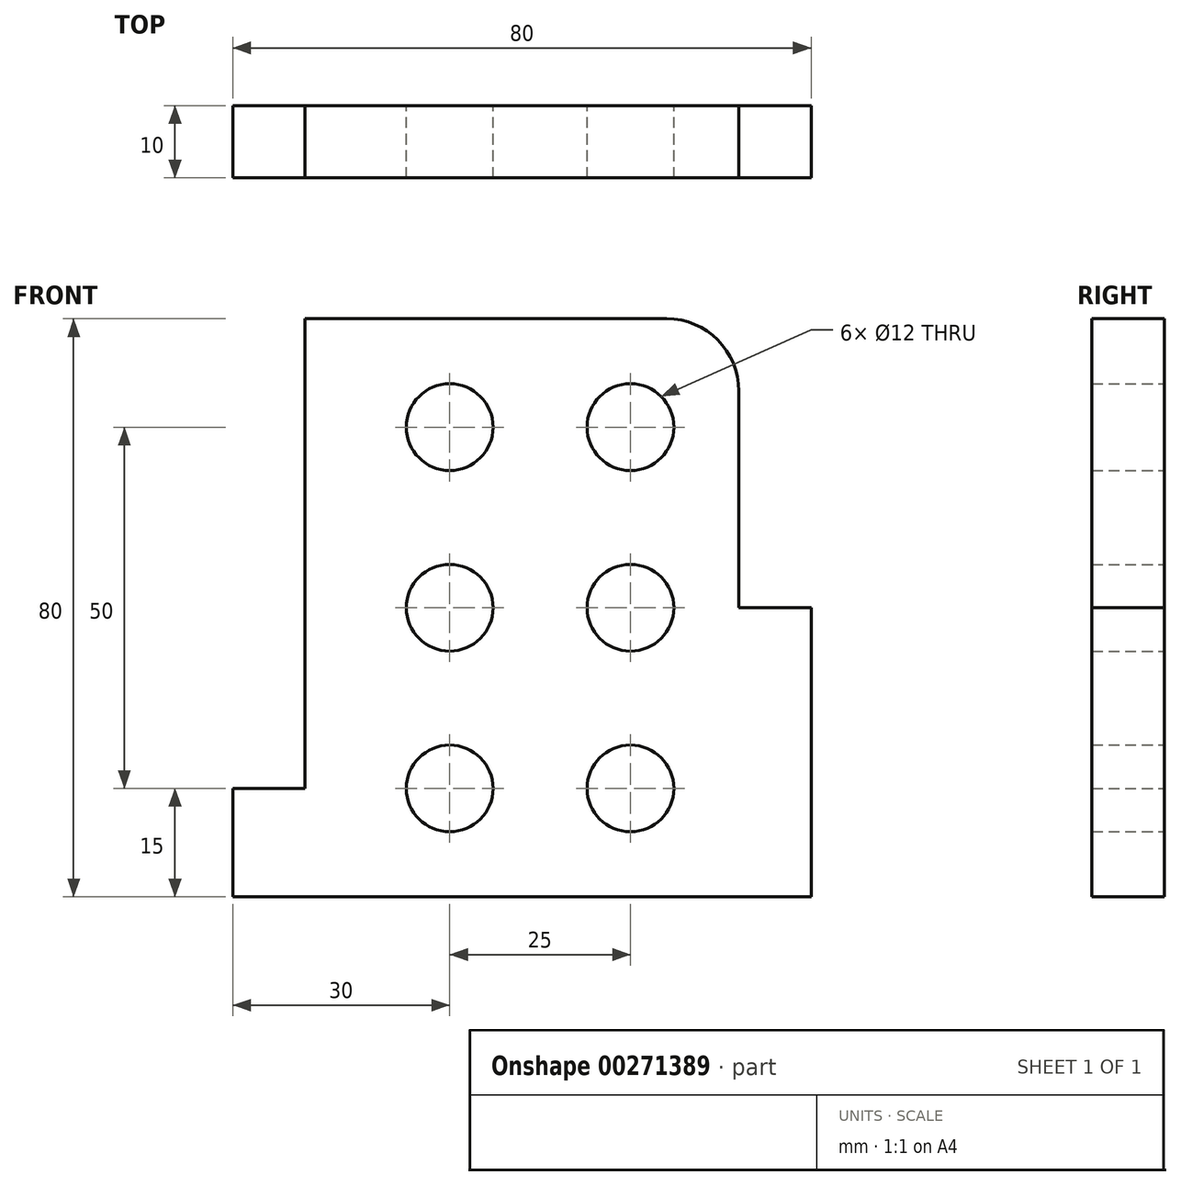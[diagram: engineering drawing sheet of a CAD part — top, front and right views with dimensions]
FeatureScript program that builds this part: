
annotation { "Feature Type Name" : "Feature", "Feature Type Description" : "" }
export const myFeature = defineFeature(function(context is Context, id is Id, definition is map)
    precondition{}
    {
        {
            var Q0;
            Q0=qCreatedBy(makeId("Front.planeOp"),FACE);
            var sketch = newSketch(context, id + "F0", { "sketchPlane" : qUnion([Q0])});
            skLineSegment(sketch, "E0", {"start": v(0, 0) * mm, "end": v(0, 15) * mm});
            skLineSegment(sketch, "E1", {"start": v(0, 15) * mm, "end": v(10, 15) * mm});
            skLineSegment(sketch, "E2", {"start": v(10, 15) * mm, "end": v(10, 80) * mm});
            skLineSegment(sketch, "E3", {"start": v(10, 80) * mm, "end": v(60, 80) * mm});
            skLineSegment(sketch, "E4", {"start": v(0, 0) * mm, "end": v(80, 0) * mm});
            skLineSegment(sketch, "E5", {"start": v(80, 0) * mm, "end": v(80, 40) * mm});
            skLineSegment(sketch, "E6", {"start": v(80, 40) * mm, "end": v(70, 40) * mm});
            skCircle(sketch, "E7", {"center": v(30, 15) * mm, "radius": 6 * mm});
            skCircle(sketch, "E8", {"center": v(55, 15) * mm, "radius": 6 * mm});
            skCircle(sketch, "E9", {"center": v(30, 40) * mm, "radius": 6 * mm});
            skCircle(sketch, "E10", {"center": v(55, 40) * mm, "radius": 6 * mm});
            skCircle(sketch, "E11", {"center": v(30, 65) * mm, "radius": 6 * mm});
            skCircle(sketch, "E12", {"center": v(55, 65) * mm, "radius": 6 * mm});
            skArc(sketch, "E13", {"start": v(70, 70) * mm, "mid": v(67.07, 77.07) * mm, "end": v(60, 80) * mm});
            skLineSegment(sketch, "E14", {"start": v(70, 70) * mm, "end": v(70, 40) * mm});
            skSolve(sketch);
        }
        {
            var Q0;
            Q0 = qSketchRegion(id + "F0", true);
            extrude(context, id + "F1", {"entities" : qUnion([Q0]), "depth" : 10 * mm});
        }
    });
